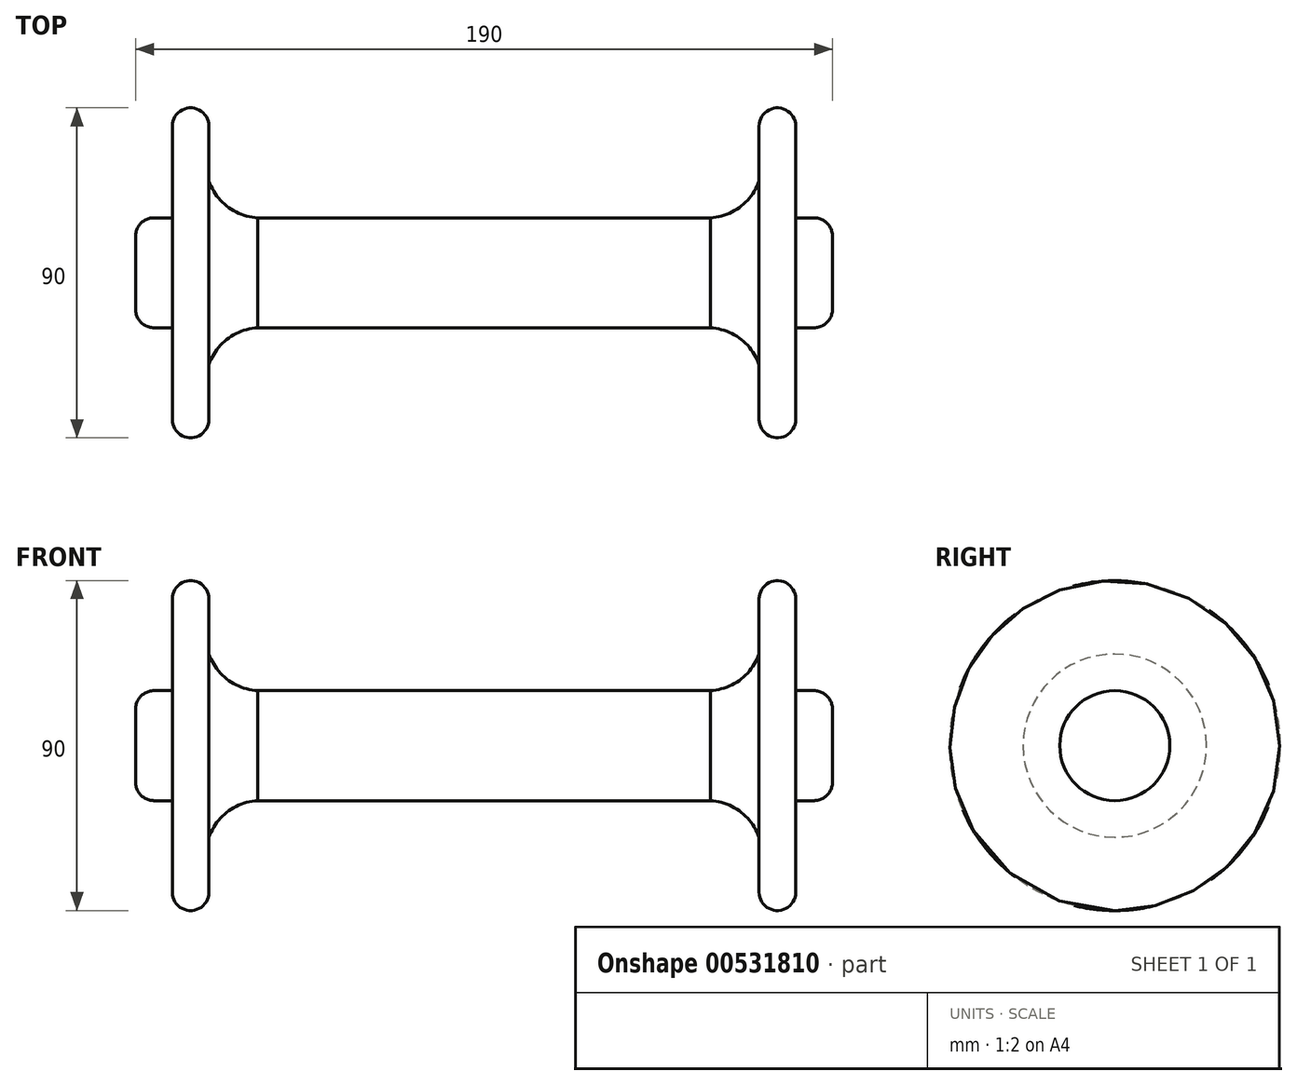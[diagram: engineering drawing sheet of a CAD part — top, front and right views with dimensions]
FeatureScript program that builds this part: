
annotation { "Feature Type Name" : "Feature", "Feature Type Description" : "" }
export const myFeature = defineFeature(function(context is Context, id is Id, definition is map)
    precondition{}
    {
        {
            var Q0;
            Q0=qCreatedBy(makeId("Front.planeOp"),FACE);
            var sketch = newSketch(context, id + "F0", { "sketchPlane" : qUnion([Q0])});
            skLineSegment(sketch, "E0", {"start": v(0, 0) * mm, "end": v(75, 0) * mm});
            skLineSegment(sketch, "E1", {"start": v(75, 0) * mm, "end": v(75, 30) * mm});
            skLineSegment(sketch, "E2", {"start": v(75, 30) * mm, "end": v(85, 30) * mm});
            skLineSegment(sketch, "E3", {"start": v(85, 30) * mm, "end": v(85, 0) * mm});
            skLineSegment(sketch, "E4", {"start": v(85, 0) * mm, "end": v(95, 0) * mm});
            skLineSegment(sketch, "E5", {"start": v(0, 0) * mm, "end": v(0, -15) * mm});
            skLineSegment(sketch, "E6", {"start": v(0, -15) * mm, "end": v(95, -15) * mm});
            skLineSegment(sketch, "E7", {"start": v(95, 0) * mm, "end": v(95, -15) * mm});
            skLineSegment(sketch, "E8", {"start": v(18.41, 0) * mm, "end": v(18.41, 10) * mm, "construction": true});
            skLineSegment(sketch, "E9", {"start": v(75, -25.5) * mm, "end": v(60, -25.5) * mm, "construction": true});
            skArc(sketch, "E10", {"start": v(60, 0) * mm, "mid": v(69.17, 2.5) * mm, "end": v(75, 10) * mm});
            skSolve(sketch);
        }
        {
            var Q0;
            Q0 = qSketchRegion(id + "F0", true);
            var Q1;
            Q1=sQuery(id+"F0.wireOp",EDGE,"E6");
            revolve(context, id + "F1", {"entities" : qUnion([Q0]), "axis" : qUnion([Q1]), "revolveType" : RevolveType.FULL});
        }
        {
            var Q0;
            Q0=makeQuery(id+"F1.opRevolve","SWEPT_EDGE",EDGE,{"disambiguationData":[OSD([sQuery(id+"F0.wireOp",EDGE,"E2"),sQuery(id+"F0.wireOp",EDGE,"E3")])]});
            var Q1;
            Q1=makeQuery(id+"F1.opRevolve","SWEPT_EDGE",EDGE,{"disambiguationData":[OSD([sQuery(id+"F0.wireOp",EDGE,"E1"),sQuery(id+"F0.wireOp",EDGE,"E2")])]});
            var Q2;
            Q2=makeQuery(id+"F1.opRevolve","SWEPT_EDGE",EDGE,{"disambiguationData":[OSD([sQuery(id+"F0.wireOp",EDGE,"E4"),sQuery(id+"F0.wireOp",EDGE,"E7")])]});
            fillet(context, id + "F2", {"entities" : qUnion([Q0, Q1, Q2]), "radius" : 5 * mm, "tangentPropagation" : true, "allowEdgeOverflow" : false});
        }
        {
            var Q0;
            Q0=makeQuery(id+"F1.opRevolve","SWEPT_BODY",BODY,{"disambiguationData":[OSD([sQuery(id+"F0.wireOp",EDGE,"E0"),sQuery(id+"F0.wireOp",EDGE,"E1"),sQuery(id+"F0.wireOp",EDGE,"E2"),sQuery(id+"F0.wireOp",EDGE,"E3"),sQuery(id+"F0.wireOp",EDGE,"E4"),sQuery(id+"F0.wireOp",EDGE,"E5"),sQuery(id+"F0.wireOp",EDGE,"E6"),sQuery(id+"F0.wireOp",EDGE,"E7"),sQuery(id+"F0.wireOp",EDGE,"E10")])]});
            var Q1;
            Q1=makeQuery(id+"F1.opRevolve","SWEPT_FACE",FACE,{"disambiguationData":[OSD([sQuery(id+"F0.wireOp",EDGE,"E5")])]});
            mirror(context, id + "F3", {"operationType" : NewBodyOperationType.ADD, "entities" : qUnion([Q0]), "mirrorPlane" : qUnion([Q1])});
        }
    });
